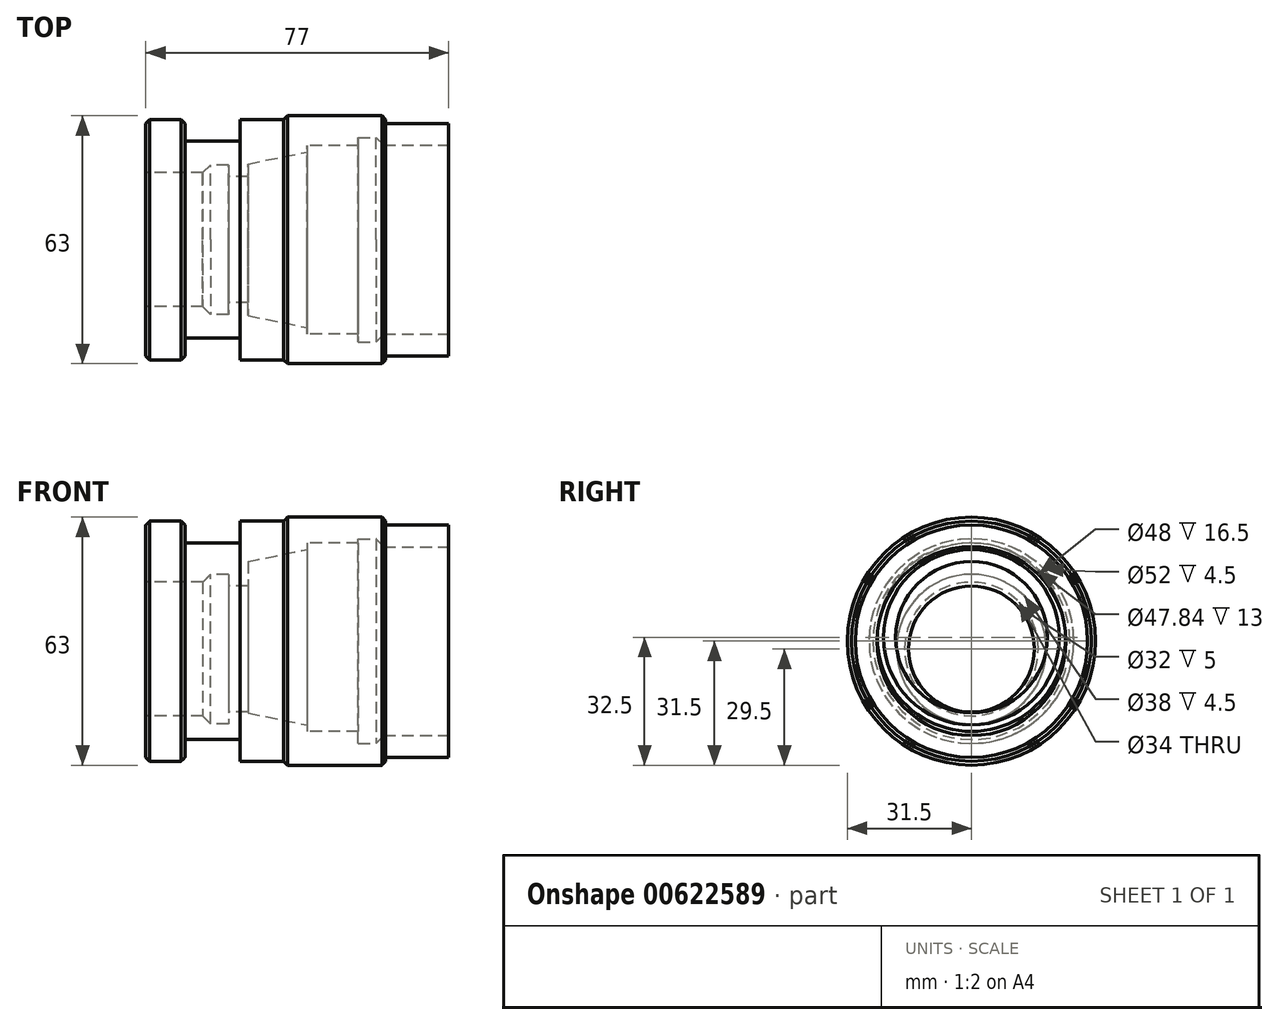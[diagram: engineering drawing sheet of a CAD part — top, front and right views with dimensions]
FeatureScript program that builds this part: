
annotation { "Feature Type Name" : "Feature", "Feature Type Description" : "" }
export const myFeature = defineFeature(function(context is Context, id is Id, definition is map)
    precondition{}
    {
        {
            var Q0;
            Q0=qCreatedBy(makeId("Front.planeOp"),FACE);
            var sketch = newSketch(context, id + "F0", { "sketchPlane" : qUnion([Q0])});
            skLineSegment(sketch, "E0", {"start": v(0, 0) * mm, "end": v(0, 30.5) * mm});
            skLineSegment(sketch, "E1", {"start": v(0, 30.5) * mm, "end": v(10, 30.5) * mm});
            skLineSegment(sketch, "E2", {"start": v(10, 30.5) * mm, "end": v(10, 25) * mm});
            skLineSegment(sketch, "E3", {"start": v(10, 25) * mm, "end": v(24, 25) * mm});
            skLineSegment(sketch, "E4", {"start": v(24, 25) * mm, "end": v(24, 30.5) * mm});
            skLineSegment(sketch, "E5", {"start": v(24, 30.5) * mm, "end": v(35, 30.5) * mm});
            skLineSegment(sketch, "E6", {"start": v(35, 30.5) * mm, "end": v(35, 31.5) * mm});
            skLineSegment(sketch, "E7", {"start": v(35, 31.5) * mm, "end": v(61, 31.5) * mm});
            skLineSegment(sketch, "E8", {"start": v(61, 31.5) * mm, "end": v(61, 29.5) * mm});
            skLineSegment(sketch, "E9", {"start": v(61, 29.5) * mm, "end": v(77, 29.5) * mm});
            skLineSegment(sketch, "E10", {"start": v(77, 29.5) * mm, "end": v(77, 0) * mm});
            skLineSegment(sketch, "E11", {"start": v(77, 0) * mm, "end": v(0, 0) * mm});
            skLineSegment(sketch, "E12", {"start": v(-8.8, 0) * mm, "end": v(74.77, 0) * mm, "construction": true});
            skSolve(sketch);
        }
        {
            var Q0;
            Q0 = qSketchRegion(id + "F0", true);
            var Q1;
            Q1=sQuery(id+"F0.wireOp",EDGE,"E12");
            revolve(context, id + "F1", {"entities" : qUnion([Q0]), "axis" : qUnion([Q1]), "revolveType" : RevolveType.FULL});
        }
        {
            var Q0;
            Q0=makeQuery(id+"F1.opRevolve","SWEPT_FACE",FACE,{"disambiguationData":[OSD([sQuery(id+"F0.wireOp",EDGE,"E1")])]});
            chamfer(context, id + "F2", {"entities" : qUnion([Q0]), "width" : 1 * mm, "tangentPropagation" : true});
        }
        {
            var Q0;
            Q0=makeQuery(id+"F1.opRevolve","SWEPT_EDGE",EDGE,{"disambiguationData":[OSD([sQuery(id+"F0.wireOp",EDGE,"E6"),sQuery(id+"F0.wireOp",EDGE,"E7")])]});
            var Q1;
            Q1=makeQuery(id+"F1.opRevolve","SWEPT_EDGE",EDGE,{"disambiguationData":[OSD([sQuery(id+"F0.wireOp",EDGE,"E7"),sQuery(id+"F0.wireOp",EDGE,"E8")])]});
            chamfer(context, id + "F3", {"entities" : qUnion([Q0, Q1]), "width" : 1 * mm, "tangentPropagation" : true});
        }
        {
            var Q0;
            Q0=qCreatedBy(makeId("Front.planeOp"),FACE);
            var sketch = newSketch(context, id + "F4", { "sketchPlane" : qUnion([Q0])});
            skLineSegment(sketch, "E13", {"start": v(54, 0) * mm, "end": v(91.68, 0) * mm, "construction": true});
            skLineSegment(sketch, "E14", {"start": v(54, 0) * mm, "end": v(54, 26) * mm});
            skLineSegment(sketch, "E15", {"start": v(54, 26) * mm, "end": v(58, 26) * mm});
            skLineSegment(sketch, "E16", {"start": v(58, 26) * mm, "end": v(58, 24) * mm});
            skLineSegment(sketch, "E17", {"start": v(58, 24) * mm, "end": v(77, 24) * mm});
            skLineSegment(sketch, "E18", {"start": v(77, 24) * mm, "end": v(77, 0) * mm});
            skLineSegment(sketch, "E19", {"start": v(77, 0) * mm, "end": v(54, 0) * mm});
            skSolve(sketch);
        }
        {
            var Q0;
            Q0 = qSketchRegion(id + "F4", true);
            var Q1;
            Q1=sQuery(id+"F4.wireOp",EDGE,"E13");
            revolve(context, id + "F5", {"operationType" : NewBodyOperationType.REMOVE, "entities" : qUnion([Q0]), "axis" : qUnion([Q1]), "revolveType" : RevolveType.FULL, "oppositeDirection" : true});
        }
        {
            var Q0;
            Q0=qCreatedBy(makeId("Front.planeOp"),FACE);
            var sketch = newSketch(context, id + "F6", { "sketchPlane" : qUnion([Q0])});
            skLineSegment(sketch, "E20", {"start": v(33.6, 1) * mm, "end": v(62.66, 1) * mm, "construction": true});
            skLineSegment(sketch, "E21", {"start": v(54, 1) * mm, "end": v(54, 24.92) * mm});
            skLineSegment(sketch, "E22", {"start": v(54, 24.92) * mm, "end": v(41, 24.92) * mm});
            skLineSegment(sketch, "E23", {"start": v(41, 24.92) * mm, "end": v(41, 23.3) * mm});
            skLineSegment(sketch, "E24", {"start": v(41, 23.3) * mm, "end": v(26, 20.25) * mm});
            skLineSegment(sketch, "E25", {"start": v(26, 20.25) * mm, "end": v(26, 1) * mm});
            skLineSegment(sketch, "E26", {"start": v(26, 1) * mm, "end": v(54, 1) * mm});
            skSolve(sketch);
        }
        {
            var Q0;
            Q0 = qSketchRegion(id + "F6", true);
            var Q1;
            Q1=sQuery(id+"F6.wireOp",EDGE,"E20");
            revolve(context, id + "F7", {"operationType" : NewBodyOperationType.REMOVE, "entities" : qUnion([Q0]), "axis" : qUnion([Q1]), "revolveType" : RevolveType.FULL});
        }
        {
            var Q0;
            Q0=qCreatedBy(makeId("Front.planeOp"),FACE);
            var sketch = newSketch(context, id + "F8", { "sketchPlane" : qUnion([Q0])});
            skLineSegment(sketch, "E27", {"start": v(-6.48, -2) * mm, "end": v(26.22, -2) * mm, "construction": true});
            skLineSegment(sketch, "E28", {"start": v(0, -2) * mm, "end": v(0, 15) * mm});
            skLineSegment(sketch, "E29", {"start": v(0, 15) * mm, "end": v(17, 15) * mm});
            skLineSegment(sketch, "E30", {"start": v(17, 15) * mm, "end": v(17, 17) * mm});
            skLineSegment(sketch, "E31", {"start": v(17, 17) * mm, "end": v(21, 17) * mm});
            skLineSegment(sketch, "E32", {"start": v(21, 17) * mm, "end": v(21, 14) * mm});
            skLineSegment(sketch, "E33", {"start": v(21, 14) * mm, "end": v(26, 14) * mm});
            skLineSegment(sketch, "E34", {"start": v(26, 14) * mm, "end": v(26, -2) * mm});
            skLineSegment(sketch, "E35", {"start": v(26, -2) * mm, "end": v(0, -2) * mm});
            skSolve(sketch);
        }
        {
            var Q0;
            Q0 = qSketchRegion(id + "F8", true);
            var Q1;
            Q1=sQuery(id+"F8.wireOp",EDGE,"E27");
            revolve(context, id + "F9", {"operationType" : NewBodyOperationType.REMOVE, "entities" : qUnion([Q0]), "axis" : qUnion([Q1]), "revolveType" : RevolveType.FULL});
        }
        {
            var Q0;
            Q0=makeQuery(id+"F9.boolean.opBoolean","COPY",EDGE,{"derivedFrom":makeQuery(id+"F9.opRevolve","SWEPT_EDGE",EDGE,{"disambiguationData":[OSD([sQuery(id+"F8.wireOp",EDGE,"E28"),sQuery(id+"F8.wireOp",EDGE,"E29")])]})});
            var Q1;
            Q1=makeQuery(id+"F9.boolean.opBoolean","COPY",EDGE,{"derivedFrom":makeQuery(id+"F9.opRevolve","SWEPT_EDGE",EDGE,{"disambiguationData":[OSD([sQuery(id+"F8.wireOp",EDGE,"E29"),sQuery(id+"F8.wireOp",EDGE,"E30")])]})});
            chamfer(context, id + "F10", {"entities" : qUnion([Q0, Q1]), "width" : 2.5 * mm, "tangentPropagation" : true});
        }
        {
            var Q0;
            Q0=makeQuery(id+"F5.boolean.opBoolean","COPY",EDGE,{"derivedFrom":makeQuery(id+"F5.opRevolve","SWEPT_EDGE",EDGE,{"disambiguationData":[OSD([sQuery(id+"F4.wireOp",EDGE,"E17"),sQuery(id+"F4.wireOp",EDGE,"E18")])]})});
            var Q1;
            Q1=makeQuery(id+"F5.boolean.opBoolean","COPY",EDGE,{"derivedFrom":makeQuery(id+"F5.opRevolve","SWEPT_EDGE",EDGE,{"disambiguationData":[OSD([sQuery(id+"F4.wireOp",EDGE,"E16"),sQuery(id+"F4.wireOp",EDGE,"E17")])]})});
            chamfer(context, id + "F11", {"entities" : qUnion([Q0, Q1]), "width" : 2.5 * mm, "tangentPropagation" : true});
        }
    });
